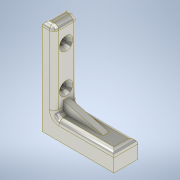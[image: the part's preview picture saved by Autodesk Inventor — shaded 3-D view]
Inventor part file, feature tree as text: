
AUTODESK INVENTOR PART (.ipt)
format: ipt  version: 2021.2 (Build 252289000, 289)  size: 173,056 bytes
history: native  units: in
note: dims shown in document units (in); Inventor stores cm internally (conversion verified against a paired STEP export)
features: sketch x4, extrude x2, hole x2, fillet x2
ambient origin geometry x8: Origin, YZ Plane, XZ Plane, XY Plane, X Axis, Y Axis, Z Axis, Center Point
bodies: Solid1 (feature_tree)
feature tree (10):
  extrude  "Extrusion1"  Depth=0.375in
  hole  "Hole1"  [1 undecoded]
  hole  "Hole2"  [1 undecoded]
  fillet  "FilletForTop"  Radius=0.4062in
  fillet  "FilletForFront"  Radius=0.4062in
  extrude  "Extrusion2"  Depth=0.125in
  sketch  "Sketch1"  dims[d0=1.5in d1=0.375in]
  sketch  "Sketch2"  dims[d2=2.0in d3=0.25in]
  sketch  "Sketch3"  dims[d4=0.5in d5=0.0in d6=0.4062in d7=0.4062in]
  sketch  "Sketch4"  dims[d8=0.15in d9=0.75in d10=0.279in d11=0.25in d12=0.5635in d13=1.0in d14=0.8108in d15=1.2in d16=0.13in d17=0.328in d18=0.279in d19=0.25in d20=0.5635in d21=0.35in d22=0.0in d24=0.1in d25=0.1in d26=0.05in d27=0.05in d28=0.125in d29=0.0in]
note: 2 required parameter values undecoded (feature->parameter linkage not recoverable at this tier; creation-order binding heuristic only, values carry confidence <= 0.55)
